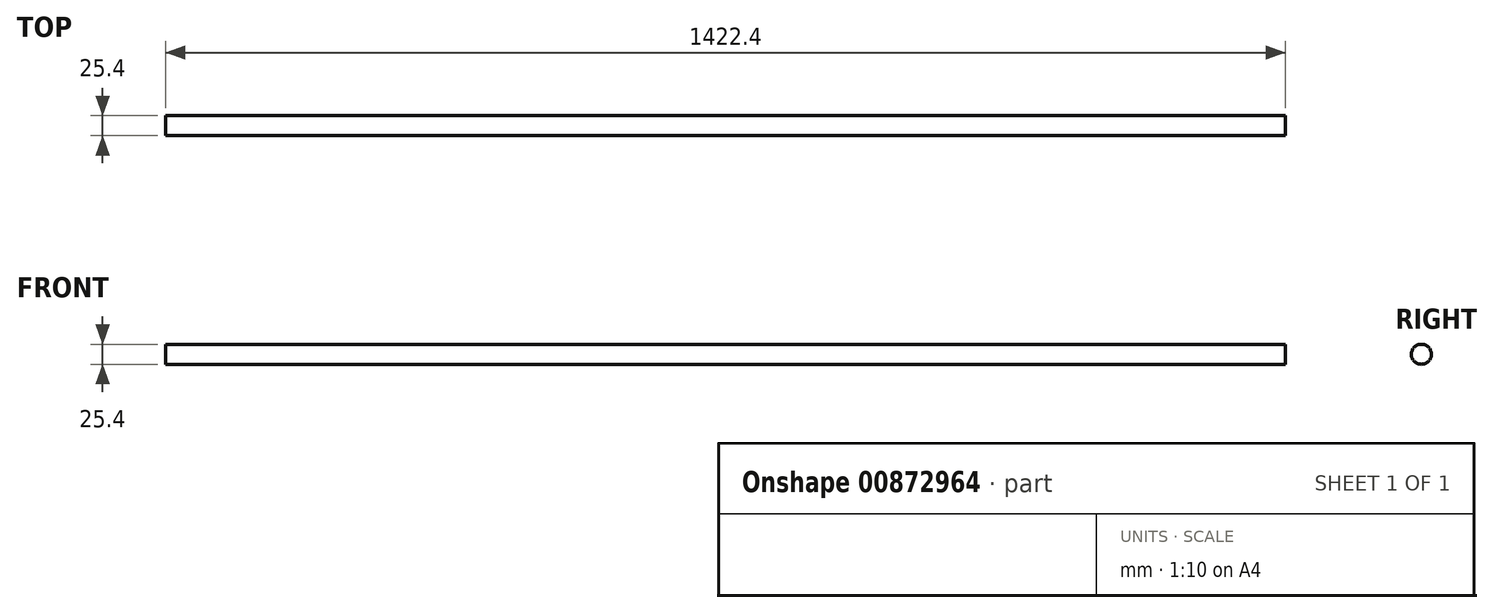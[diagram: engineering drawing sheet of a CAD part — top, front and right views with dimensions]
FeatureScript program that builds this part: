
annotation { "Feature Type Name" : "Feature", "Feature Type Description" : "" }
export const myFeature = defineFeature(function(context is Context, id is Id, definition is map)
    precondition{}
    {
        {
            var Q0;
            Q0=qCreatedBy(makeId("Right.planeOp"),FACE);
            var sketch = newSketch(context, id + "F0", { "sketchPlane" : qUnion([Q0])});
            skCircle(sketch, "E0", {"center": v(0, 0) * mm, "radius": 12.7 * mm});
            skSolve(sketch);
        }
        {
            var Q0;
            Q0 = qSketchRegion(id + "F0", true);
            extrude(context, id + "F1", {"entities" : qUnion([Q0]), "depth" : 1422.4 * mm, "offsetDistance" : 25.4 * mm});
        }
    });
